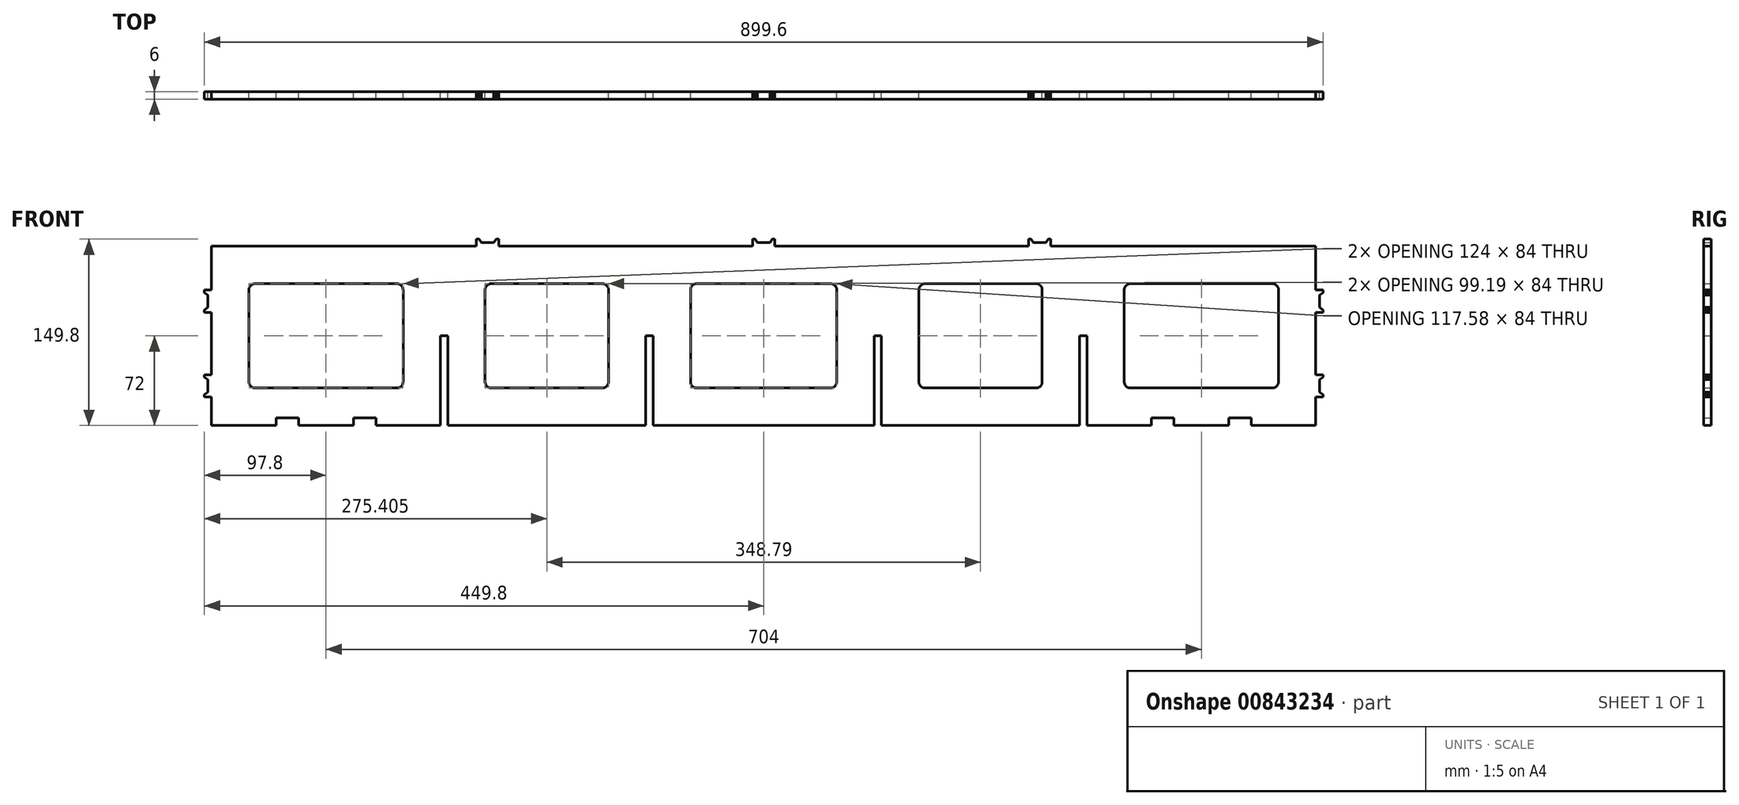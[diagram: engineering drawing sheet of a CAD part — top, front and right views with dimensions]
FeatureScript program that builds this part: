
annotation { "Feature Type Name" : "Feature", "Feature Type Description" : "" }
export const myFeature = defineFeature(function(context is Context, id is Id, definition is map)
    precondition{}
    {
        {
            var Q0;
            Q0=qCreatedBy(makeId("Front.planeOp"),FACE);
            var sketch = newSketch(context, id + "F0", { "sketchPlane" : qUnion([Q0])});
            skLineSegment(sketch, "E0.top", {"start": v(0, -144) * mm, "end": v(52, -144) * mm});
            skLineSegment(sketch, "E0.left", {"start": v(0, 0) * mm, "end": v(0, -35.2) * mm});
            skLineSegment(sketch, "E0.right", {"start": v(888, 0) * mm, "end": v(888, -35.2) * mm});
            skLineSegment(sketch, "E1", {"start": v(213, 0) * mm, "end": v(213, 5.8) * mm});
            skLineSegment(sketch, "E2", {"start": v(213, 5.8) * mm, "end": v(215, 5.8) * mm});
            skLineSegment(sketch, "E3", {"start": v(215, 5.8) * mm, "end": v(217, 3) * mm});
            skLineSegment(sketch, "E4", {"start": v(217, 3) * mm, "end": v(227, 3) * mm});
            skLineSegment(sketch, "E5", {"start": v(227, 3) * mm, "end": v(229, 5.8) * mm});
            skLineSegment(sketch, "E6", {"start": v(229, 5.8) * mm, "end": v(231, 5.8) * mm});
            skLineSegment(sketch, "E7", {"start": v(231, 5.8) * mm, "end": v(231, 0) * mm});
            skLineSegment(sketch, "E8", {"start": v(435, 0) * mm, "end": v(435, 5.8) * mm});
            skLineSegment(sketch, "E9", {"start": v(435, 5.8) * mm, "end": v(437, 5.8) * mm});
            skLineSegment(sketch, "E10", {"start": v(437, 5.8) * mm, "end": v(439, 3) * mm});
            skLineSegment(sketch, "E11", {"start": v(439, 3) * mm, "end": v(449, 3) * mm});
            skLineSegment(sketch, "E12", {"start": v(449, 3) * mm, "end": v(451, 5.8) * mm});
            skLineSegment(sketch, "E13", {"start": v(451, 5.8) * mm, "end": v(453, 5.8) * mm});
            skLineSegment(sketch, "E14", {"start": v(453, 5.8) * mm, "end": v(453, 0) * mm});
            skLineSegment(sketch, "E15", {"start": v(657, 0) * mm, "end": v(657, 5.8) * mm});
            skLineSegment(sketch, "E16", {"start": v(657, 5.8) * mm, "end": v(659, 5.8) * mm});
            skLineSegment(sketch, "E17", {"start": v(659, 5.8) * mm, "end": v(661, 3) * mm});
            skLineSegment(sketch, "E18", {"start": v(661, 3) * mm, "end": v(671, 3) * mm});
            skLineSegment(sketch, "E19", {"start": v(671, 3) * mm, "end": v(673, 5.8) * mm});
            skLineSegment(sketch, "E20", {"start": v(673, 5.8) * mm, "end": v(675, 5.8) * mm});
            skLineSegment(sketch, "E21", {"start": v(675, 5.8) * mm, "end": v(675, 0) * mm});
            skLineSegment(sketch, "E22", {"start": v(0, -35.2) * mm, "end": v(-5.8, -35.2) * mm});
            skLineSegment(sketch, "E23", {"start": v(-5.8, -35.2) * mm, "end": v(-5.8, -37.2) * mm});
            skLineSegment(sketch, "E24", {"start": v(-5.8, -37.2) * mm, "end": v(-3, -39.2) * mm});
            skLineSegment(sketch, "E25", {"start": v(-3, -39.2) * mm, "end": v(-3, -49.2) * mm});
            skLineSegment(sketch, "E26", {"start": v(-3, -49.2) * mm, "end": v(-5.8, -51.21) * mm});
            skLineSegment(sketch, "E27", {"start": v(-5.8, -51.21) * mm, "end": v(-5.8, -53.21) * mm});
            skLineSegment(sketch, "E28", {"start": v(-5.8, -53.21) * mm, "end": v(0, -53.21) * mm});
            skLineSegment(sketch, "E29", {"start": v(0, -103.23) * mm, "end": v(-5.8, -103.23) * mm});
            skLineSegment(sketch, "E30", {"start": v(-5.8, -103.23) * mm, "end": v(-5.8, -105.23) * mm});
            skLineSegment(sketch, "E31", {"start": v(-5.8, -105.23) * mm, "end": v(-3, -107.23) * mm});
            skLineSegment(sketch, "E32", {"start": v(-3, -107.23) * mm, "end": v(-3, -117.23) * mm});
            skLineSegment(sketch, "E33", {"start": v(-3, -117.23) * mm, "end": v(-5.8, -119.23) * mm});
            skLineSegment(sketch, "E34", {"start": v(-5.8, -119.23) * mm, "end": v(-5.8, -121.23) * mm});
            skLineSegment(sketch, "E35", {"start": v(-5.8, -121.23) * mm, "end": v(0, -121.23) * mm});
            skLineSegment(sketch, "E36.trimOffspring", {"start": v(0, -53.21) * mm, "end": v(0, -103.23) * mm});
            skLineSegment(sketch, "E37", {"start": v(888, -35.2) * mm, "end": v(893.8, -35.2) * mm});
            skLineSegment(sketch, "E38", {"start": v(893.8, -35.2) * mm, "end": v(893.8, -37.2) * mm});
            skLineSegment(sketch, "E39", {"start": v(893.8, -37.21) * mm, "end": v(891, -39.2) * mm});
            skLineSegment(sketch, "E40", {"start": v(891, -39.2) * mm, "end": v(891, -49.2) * mm});
            skLineSegment(sketch, "E41", {"start": v(891, -49.2) * mm, "end": v(893.8, -51.2) * mm});
            skLineSegment(sketch, "E42", {"start": v(893.8, -51.2) * mm, "end": v(893.8, -53.2) * mm});
            skLineSegment(sketch, "E43", {"start": v(893.8, -53.2) * mm, "end": v(888, -53.2) * mm});
            skLineSegment(sketch, "E44.trimOffspring", {"start": v(888, -53.2) * mm, "end": v(888, -103.23) * mm});
            skLineSegment(sketch, "E45", {"start": v(888, -103.23) * mm, "end": v(893.8, -103.23) * mm});
            skLineSegment(sketch, "E46", {"start": v(893.8, -103.23) * mm, "end": v(893.8, -105.23) * mm});
            skLineSegment(sketch, "E47", {"start": v(893.8, -105.23) * mm, "end": v(891, -107.23) * mm});
            skLineSegment(sketch, "E48", {"start": v(891, -107.23) * mm, "end": v(891, -117.23) * mm});
            skLineSegment(sketch, "E49", {"start": v(891, -117.23) * mm, "end": v(893.8, -119.23) * mm});
            skLineSegment(sketch, "E50", {"start": v(893.8, -119.23) * mm, "end": v(893.8, -121.23) * mm});
            skLineSegment(sketch, "E51", {"start": v(893.8, -121.23) * mm, "end": v(888, -121.23) * mm});
            skLineSegment(sketch, "E52.trimOffspring", {"start": v(0, -121.23) * mm, "end": v(0, -144) * mm});
            skLineSegment(sketch, "E53.trimOffspring", {"start": v(888, -121.23) * mm, "end": v(888, -144) * mm});
            skLineSegment(sketch, "E54", {"start": v(0, 0) * mm, "end": v(213, 0) * mm});
            skLineSegment(sketch, "E55", {"start": v(231, 0) * mm, "end": v(435, 0) * mm});
            skLineSegment(sketch, "E56", {"start": v(184, -144) * mm, "end": v(184, -71.99) * mm});
            skLineSegment(sketch, "E57", {"start": v(184, -71.99) * mm, "end": v(190, -71.99) * mm});
            skLineSegment(sketch, "E58", {"start": v(190, -71.99) * mm, "end": v(190, -144) * mm});
            skLineSegment(sketch, "E59", {"start": v(349.2, -144) * mm, "end": v(349.2, -71.99) * mm});
            skLineSegment(sketch, "E60", {"start": v(349.2, -71.99) * mm, "end": v(355.2, -71.99) * mm});
            skLineSegment(sketch, "E61", {"start": v(355.2, -71.99) * mm, "end": v(355.2, -144) * mm});
            skLineSegment(sketch, "E62", {"start": v(453, 0) * mm, "end": v(657, 0) * mm});
            skLineSegment(sketch, "E63", {"start": v(532.8, -144) * mm, "end": v(532.8, -71.99) * mm});
            skLineSegment(sketch, "E64", {"start": v(532.8, -71.99) * mm, "end": v(538.8, -71.99) * mm});
            skLineSegment(sketch, "E65", {"start": v(538.8, -71.99) * mm, "end": v(538.8, -144) * mm});
            skLineSegment(sketch, "E66", {"start": v(675, 0) * mm, "end": v(888, 0) * mm});
            skLineSegment(sketch, "E67", {"start": v(698, -144) * mm, "end": v(698, -71.99) * mm});
            skLineSegment(sketch, "E68", {"start": v(698, -71.99) * mm, "end": v(704, -71.99) * mm});
            skLineSegment(sketch, "E69", {"start": v(704, -71.99) * mm, "end": v(704, -144) * mm});
            skLineSegment(sketch, "E70.trimOffspring", {"start": v(355.2, -144) * mm, "end": v(532.8, -144) * mm});
            skLineSegment(sketch, "E71.trimOffspring", {"start": v(538.8, -144) * mm, "end": v(698, -144) * mm});
            skLineSegment(sketch, "E72.trimOffspring", {"start": v(704, -144) * mm, "end": v(755.9, -144) * mm});
            skLineSegment(sketch, "E73.trimOffspring", {"start": v(190, -144) * mm, "end": v(349.2, -144) * mm});
            skLineSegment(sketch, "E74", {"start": v(35, -30) * mm, "end": v(149, -30) * mm});
            skLineSegment(sketch, "E75", {"start": v(154, -35) * mm, "end": v(154, -109) * mm});
            skLineSegment(sketch, "E76", {"start": v(149, -114) * mm, "end": v(35, -114) * mm});
            skLineSegment(sketch, "E77", {"start": v(30, -109) * mm, "end": v(30, -35) * mm});
            skLineSegment(sketch, "E78", {"start": v(220, -35) * mm, "end": v(220, -109) * mm});
            skLineSegment(sketch, "E79", {"start": v(225, -114) * mm, "end": v(314.2, -114) * mm});
            skLineSegment(sketch, "E80", {"start": v(319.2, -109) * mm, "end": v(319.2, -35) * mm});
            skLineSegment(sketch, "E81", {"start": v(314.2, -30) * mm, "end": v(225, -30) * mm});
            skLineSegment(sketch, "E82", {"start": v(385.2, -35) * mm, "end": v(385.2, -109) * mm});
            skLineSegment(sketch, "E83", {"start": v(390.2, -114) * mm, "end": v(497.79, -114) * mm});
            skLineSegment(sketch, "E84", {"start": v(502.79, -109) * mm, "end": v(502.79, -35) * mm});
            skLineSegment(sketch, "E85", {"start": v(497.79, -30) * mm, "end": v(390.2, -30) * mm});
            skLineSegment(sketch, "E86", {"start": v(568.8, -35) * mm, "end": v(568.8, -109) * mm});
            skLineSegment(sketch, "E87", {"start": v(573.8, -114) * mm, "end": v(663, -114) * mm});
            skLineSegment(sketch, "E88", {"start": v(668, -109) * mm, "end": v(668, -35) * mm});
            skLineSegment(sketch, "E89", {"start": v(663, -30) * mm, "end": v(573.8, -30) * mm});
            skLineSegment(sketch, "E90", {"start": v(734, -35) * mm, "end": v(734, -109) * mm});
            skLineSegment(sketch, "E91", {"start": v(739, -114) * mm, "end": v(853, -114) * mm});
            skLineSegment(sketch, "E92", {"start": v(858, -109) * mm, "end": v(858, -35) * mm});
            skLineSegment(sketch, "E93", {"start": v(853, -30) * mm, "end": v(739, -30) * mm});
            skPoint(sketch, "E94.visualSharp", {"position": v(30, -30) * mm});
            skArc(sketch, "E94.filletArc", {"start": v(35, -30) * mm, "mid": v(31.46, -31.46) * mm, "end": v(30, -35) * mm});
            skPoint(sketch, "E95.visualSharp", {"position": v(154, -30) * mm});
            skArc(sketch, "E95.filletArc", {"start": v(154, -35) * mm, "mid": v(152.54, -31.46) * mm, "end": v(149, -30) * mm});
            skPoint(sketch, "E96.visualSharp", {"position": v(30, -114) * mm});
            skArc(sketch, "E96.filletArc", {"start": v(30, -109) * mm, "mid": v(31.46, -112.54) * mm, "end": v(35, -114) * mm});
            skPoint(sketch, "E97.visualSharp", {"position": v(154, -114) * mm});
            skArc(sketch, "E97.filletArc", {"start": v(149, -114) * mm, "mid": v(152.54, -112.54) * mm, "end": v(154, -109) * mm});
            skPoint(sketch, "E98.visualSharp", {"position": v(220, -30) * mm});
            skArc(sketch, "E98.filletArc", {"start": v(225, -30) * mm, "mid": v(221.47, -31.46) * mm, "end": v(220, -35) * mm});
            skPoint(sketch, "E99.visualSharp", {"position": v(220, -114) * mm});
            skArc(sketch, "E99.filletArc", {"start": v(220, -109) * mm, "mid": v(221.47, -112.54) * mm, "end": v(225, -114) * mm});
            skPoint(sketch, "E100.visualSharp", {"position": v(319.2, -114) * mm});
            skArc(sketch, "E100.filletArc", {"start": v(314.2, -114) * mm, "mid": v(317.74, -112.54) * mm, "end": v(319.2, -109) * mm});
            skPoint(sketch, "E101.visualSharp", {"position": v(319.2, -30) * mm});
            skArc(sketch, "E101.filletArc", {"start": v(319.2, -35) * mm, "mid": v(317.74, -31.46) * mm, "end": v(314.2, -30) * mm});
            skPoint(sketch, "E102.visualSharp", {"position": v(385.2, -30) * mm});
            skArc(sketch, "E102.filletArc", {"start": v(390.2, -30) * mm, "mid": v(386.67, -31.46) * mm, "end": v(385.2, -35) * mm});
            skPoint(sketch, "E103.visualSharp", {"position": v(385.2, -114) * mm});
            skArc(sketch, "E103.filletArc", {"start": v(385.2, -109) * mm, "mid": v(386.67, -112.54) * mm, "end": v(390.2, -114) * mm});
            skPoint(sketch, "E104.visualSharp", {"position": v(502.79, -30) * mm});
            skArc(sketch, "E104.filletArc", {"start": v(502.79, -35) * mm, "mid": v(501.33, -31.46) * mm, "end": v(497.79, -30) * mm});
            skPoint(sketch, "E105.visualSharp", {"position": v(502.79, -114) * mm});
            skArc(sketch, "E105.filletArc", {"start": v(497.79, -114) * mm, "mid": v(501.33, -112.54) * mm, "end": v(502.79, -109) * mm});
            skPoint(sketch, "E106.visualSharp", {"position": v(568.8, -114) * mm});
            skArc(sketch, "E106.filletArc", {"start": v(568.8, -109) * mm, "mid": v(570.26, -112.54) * mm, "end": v(573.8, -114) * mm});
            skPoint(sketch, "E107.visualSharp", {"position": v(568.8, -30) * mm});
            skArc(sketch, "E107.filletArc", {"start": v(573.8, -30) * mm, "mid": v(570.26, -31.46) * mm, "end": v(568.8, -35) * mm});
            skPoint(sketch, "E108.visualSharp", {"position": v(668, -30) * mm});
            skArc(sketch, "E108.filletArc", {"start": v(667.99, -35) * mm, "mid": v(666.53, -31.46) * mm, "end": v(663, -30) * mm});
            skPoint(sketch, "E109.visualSharp", {"position": v(668, -114) * mm});
            skArc(sketch, "E109.filletArc", {"start": v(663, -114) * mm, "mid": v(666.53, -112.54) * mm, "end": v(668, -109) * mm});
            skPoint(sketch, "E110.visualSharp", {"position": v(734, -30) * mm});
            skArc(sketch, "E110.filletArc", {"start": v(739, -30) * mm, "mid": v(735.46, -31.46) * mm, "end": v(734, -35) * mm});
            skPoint(sketch, "E111.visualSharp", {"position": v(734, -114) * mm});
            skArc(sketch, "E111.filletArc", {"start": v(734, -109) * mm, "mid": v(735.46, -112.54) * mm, "end": v(739, -114) * mm});
            skPoint(sketch, "E112.visualSharp", {"position": v(858, -30) * mm});
            skArc(sketch, "E112.filletArc", {"start": v(858, -35) * mm, "mid": v(856.54, -31.46) * mm, "end": v(853, -30) * mm});
            skPoint(sketch, "E113.visualSharp", {"position": v(858, -114) * mm});
            skArc(sketch, "E113.filletArc", {"start": v(853, -114) * mm, "mid": v(856.54, -112.54) * mm, "end": v(858, -109) * mm});
            skLineSegment(sketch, "E114", {"start": v(52, -144) * mm, "end": v(52, -137.99) * mm});
            skLineSegment(sketch, "E115", {"start": v(52, -137.99) * mm, "end": v(70.1, -137.99) * mm});
            skLineSegment(sketch, "E116", {"start": v(70.1, -137.99) * mm, "end": v(70.1, -144) * mm});
            skLineSegment(sketch, "E117", {"start": v(114, -144) * mm, "end": v(114, -137.99) * mm});
            skLineSegment(sketch, "E118", {"start": v(114, -137.99) * mm, "end": v(132.1, -137.99) * mm});
            skLineSegment(sketch, "E119", {"start": v(132.1, -138) * mm, "end": v(132.1, -144) * mm});
            skLineSegment(sketch, "E120", {"start": v(755.9, -144) * mm, "end": v(755.9, -137.99) * mm});
            skLineSegment(sketch, "E121", {"start": v(755.9, -137.99) * mm, "end": v(774, -137.99) * mm});
            skLineSegment(sketch, "E122", {"start": v(774, -137.99) * mm, "end": v(774, -144) * mm});
            skLineSegment(sketch, "E123", {"start": v(817.9, -144) * mm, "end": v(817.9, -137.99) * mm});
            skLineSegment(sketch, "E124", {"start": v(817.9, -137.99) * mm, "end": v(836, -137.99) * mm});
            skLineSegment(sketch, "E125", {"start": v(836, -137.99) * mm, "end": v(836, -144) * mm});
            skLineSegment(sketch, "E126.trimOffspring", {"start": v(70.1, -144) * mm, "end": v(114, -144) * mm});
            skLineSegment(sketch, "E127.trimOffspring", {"start": v(132.1, -144) * mm, "end": v(184, -144) * mm});
            skLineSegment(sketch, "E128.trimOffspring", {"start": v(774, -144) * mm, "end": v(817.9, -144) * mm});
            skLineSegment(sketch, "E129.trimOffspring", {"start": v(836, -144) * mm, "end": v(888, -144) * mm});
            skSolve(sketch);
        }
        {
            var Q0;
            Q0 = qSketchRegion(id + "F0", true);
            extrude(context, id + "F1", {"entities" : qUnion([Q0]), "depth" : 6 * mm, "offsetDistance" : 25 * mm});
        }
    });
